# Revit family: TESK_Насос вертикальный_SVH(T) 64
name_source: partatom
category: Оборудование
units: mm (PartAtom-declared; Revit-internal decimal feet)

## family parameters
Всегда вертикально = Да
Классификация = Насос
На основе рабочей плоскости = Нет
Общий = Нет
При загрузке вырезать с полостями = Нет
Размер круглого соединителя = Использовать диаметр
Тип детали = Вставляется
Точка расчета площади = Нет

## types (1)
- Загрузите каталог типоразмеров TXT
    ADSK_Версия Revit = 2019
    ADSK_Версия семейства = 1.0
    ADSK_Диаметр условный = 100 мм
    ADSK_Единица измерения = шт.
    ADSK_Завод-изготовитель = TESK
    ADSK_Классификация нагрузок = Прочее
    ADSK_Код изделия = Не найдено: Насос TESK SVH(T) 64
    ADSK_Количество = 1
    ADSK_Количество фаз = 3
    ADSK_Количество фаз числовое = 3
    ADSK_Коэффициент мощности = 1
    ADSK_Марка = Загрузите каталог типоразмеров TXT
    ADSK_Масса = 0
    ADSK_Масса_Текст = Не найдено: Насос TESK SVH(T) 64
    ADSK_Наименование = Не найдено: Насос TESK SVH(T) 64
    ADSK_Наименование краткое = Вертикальный многоступенчатый центробежный насос
    ADSK_Напряжение = 400 В
    ADSK_Номинальная мощность = 0 кВт
    ADSK_Полная мощность = 0 кВ·А
    ADSK_Ток = 0 А
    B1 = 519 мм
    B2 = 465 мм
    D1 = 260 мм
    D2 = 210 мм
    DN = 100 мм
    URL = www.teskpump.ru
    d фланца = 150 мм
    d1 = 216 мм
    d2 = 201 мм
    d21 = 199 мм
    h1 = 12 мм
    h2 = 135 мм
    h3 = 16 мм
    r = 25 мм
    x1 = 59 мм
    x2 = 80 мм
    Высота_Перехода = 197 мм
    Длина_ВспомЛиния = 30 мм
    Изготовитель = TESK
    Материал_1 = TESK_Серо-зеленый_Условный
    Материал_2 = TESK_Нержавеющая сталь
    Материал_3 = TESK_Чугун_Окрашенный серо-зеленый
    Материал_КорпусДвигателя = TESK_Серо-зеленый_Ребра_Условный
    Материал_КорпусУлитка = TESK_Нержавеющая сталь
    Модель = TESK SVH(T) 64
    Напор максимальный = 0
    Описание = Вертикальный многоступенчатый центробежный насос
    УГО_Длина = 365 мм
    Фланец_Толщина = 28 мм
